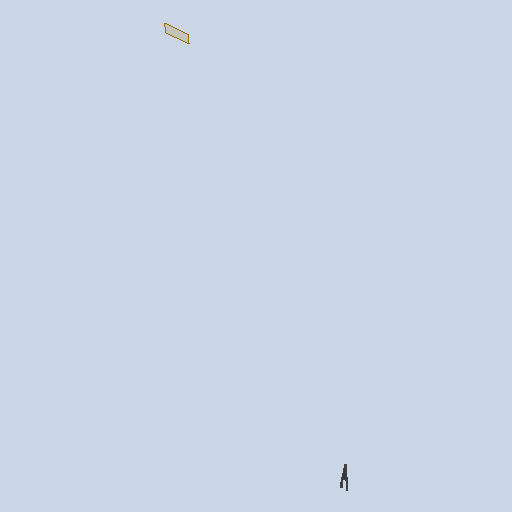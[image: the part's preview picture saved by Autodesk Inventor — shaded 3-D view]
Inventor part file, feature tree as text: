
AUTODESK INVENTOR PART (.ipt)
format: ipt  version: 2025.2 (Build 292293000, 293)  size: 99,328 bytes
history: native  units: in
note: dims shown in document units (in); Inventor stores cm internally (conversion verified against a paired STEP export)
features: reference x5, other x4, plane x1, extrude x1, sketch x1
ambient origin geometry x8: Origin, YZ Plane, XZ Plane, XY Plane, X Axis, Y Axis, Z Axis, Center Point
bodies: Solid1 (feature_tree)
feature tree (12):
  plane  "Work Plane1"
  extrude  "Extrusion1"  [1 undecoded]
  sketch  "Sketch1"  dims[d0=0.0787in d1=0.0in]
  reference  "Reference1"
  reference  "Reference2"
  reference  "Reference3"
  reference  "Reference4"
  reference  "Reference5"
  other  "<userpath>\Downloads\UAV_v0.2.0\UAV_v0.2.0\UAV_Assembly.iam"
  other  "UAV_Assembly.iam"
  other  "MiddleWingL:1"
  other  "KST_DS215MG:1"
note: 1 required parameter value undecoded (feature->parameter linkage not recoverable at this tier; creation-order binding heuristic only, values carry confidence <= 0.55)
